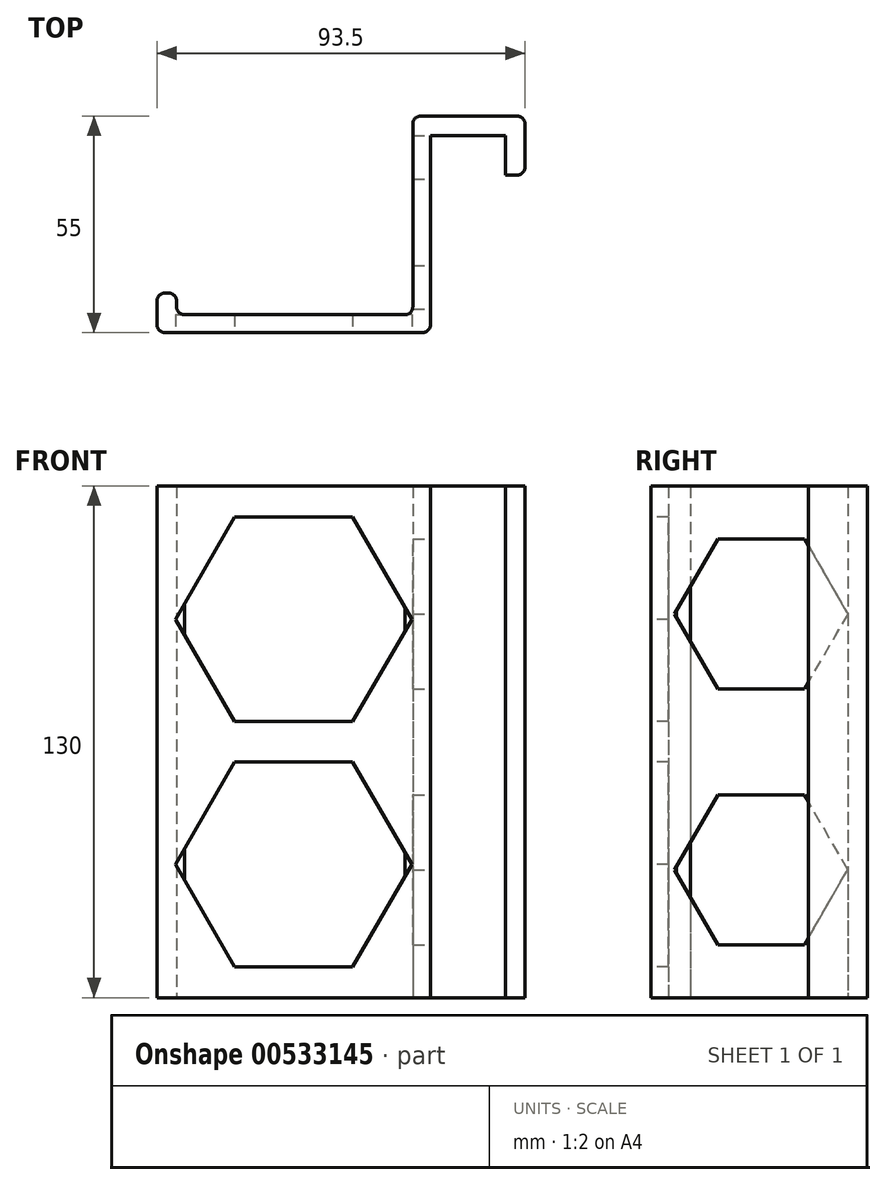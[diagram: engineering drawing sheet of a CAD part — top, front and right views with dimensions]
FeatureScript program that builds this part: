
annotation { "Feature Type Name" : "Feature", "Feature Type Description" : "" }
export const myFeature = defineFeature(function(context is Context, id is Id, definition is map)
    precondition{}
    {
        {
            var Q0;
            Q0=qCreatedBy(makeId("Top.planeOp"),FACE);
            var sketch = newSketch(context, id + "F0", { "sketchPlane" : qUnion([Q0])});
            skLineSegment(sketch, "E0.bottom", {"start": v(0, 0) * mm, "end": v(2, 0) * mm});
            skLineSegment(sketch, "E0.top", {"start": v(-2.5, 51.6) * mm, "end": v(0, 51.6) * mm});
            skLineSegment(sketch, "E0.left", {"start": v(-4.5, 3.12) * mm, "end": v(-4.5, 49.6) * mm});
            skLineSegment(sketch, "E1.bottom", {"start": v(0, 51.6) * mm, "end": v(19, 51.6) * mm});
            skLineSegment(sketch, "E1.top", {"start": v(0, 46.6) * mm, "end": v(19, 46.6) * mm});
            skLineSegment(sketch, "E1.left", {"start": v(0, 51.6) * mm, "end": v(0, 46.6) * mm});
            skLineSegment(sketch, "E1.right", {"start": v(19, 51.6) * mm, "end": v(19, 46.6) * mm});
            skLineSegment(sketch, "E2.bottom", {"start": v(19, 51.6) * mm, "end": v(22, 51.6) * mm});
            skLineSegment(sketch, "E2.top", {"start": v(19, 36.6) * mm, "end": v(22, 36.6) * mm});
            skLineSegment(sketch, "E2.left", {"start": v(19, 51.6) * mm, "end": v(19, 36.6) * mm});
            skLineSegment(sketch, "E2.right", {"start": v(24, 49.6) * mm, "end": v(24, 38.6) * mm});
            skLineSegment(sketch, "E3.bottom", {"start": v(-6.5, 1.12) * mm, "end": v(-62.5, 1.12) * mm});
            skLineSegment(sketch, "E4.bottom", {"start": v(-2, -3.4) * mm, "end": v(-67.5, -3.4) * mm});
            skLineSegment(sketch, "E4.top", {"start": v(-66.5, 6.6) * mm, "end": v(-67.5, 6.6) * mm});
            skLineSegment(sketch, "E4.left", {"start": v(-64.5, 3.12) * mm, "end": v(-64.5, 4.6) * mm});
            skLineSegment(sketch, "E4.right", {"start": v(-69.5, -1.4) * mm, "end": v(-69.5, 4.6) * mm});
            skPoint(sketch, "E5.visualSharp", {"position": v(-69.5, -3.4) * mm});
            skArc(sketch, "E5.filletArc", {"start": v(-69.5, -1.4) * mm, "mid": v(-68.91, -2.8) * mm, "end": v(-67.5, -3.4) * mm});
            skPoint(sketch, "E6.visualSharp", {"position": v(-69.5, 6.6) * mm});
            skArc(sketch, "E6.filletArc", {"start": v(-67.5, 6.6) * mm, "mid": v(-68.91, 6.02) * mm, "end": v(-69.5, 4.6) * mm});
            skPoint(sketch, "E7.visualSharp", {"position": v(-4.5, 51.6) * mm});
            skArc(sketch, "E7.filletArc", {"start": v(-2.5, 51.6) * mm, "mid": v(-3.91, 51.02) * mm, "end": v(-4.5, 49.6) * mm});
            skPoint(sketch, "E8.visualSharp", {"position": v(24, 51.6) * mm});
            skArc(sketch, "E8.filletArc", {"start": v(24, 49.6) * mm, "mid": v(23.41, 51.02) * mm, "end": v(22, 51.6) * mm});
            skPoint(sketch, "E9.visualSharp", {"position": v(24, 36.6) * mm});
            skArc(sketch, "E9.filletArc", {"start": v(22, 36.6) * mm, "mid": v(23.41, 37.2) * mm, "end": v(24, 38.6) * mm});
            skPoint(sketch, "E10.visualSharp", {"position": v(-64.5, 6.6) * mm});
            skArc(sketch, "E10.filletArc", {"start": v(-64.5, 4.6) * mm, "mid": v(-65.09, 6.02) * mm, "end": v(-66.5, 6.6) * mm});
            skLineSegment(sketch, "E11", {"start": v(0, 46.6) * mm, "end": v(0, -1.4) * mm});
            skPoint(sketch, "E12.visualSharp", {"position": v(-64.5, 1.12) * mm});
            skArc(sketch, "E12.filletArc", {"start": v(-64.5, 3.12) * mm, "mid": v(-63.91, 1.7) * mm, "end": v(-62.5, 1.12) * mm});
            skPoint(sketch, "E13.visualSharp", {"position": v(-4.5, 1.12) * mm});
            skArc(sketch, "E13.filletArc", {"start": v(-6.5, 1.12) * mm, "mid": v(-5.09, 1.7) * mm, "end": v(-4.5, 3.12) * mm});
            skPoint(sketch, "E14.visualSharp", {"position": v(0, -3.4) * mm});
            skArc(sketch, "E14.filletArc", {"start": v(-2, -3.4) * mm, "mid": v(-0.59, -2.8) * mm, "end": v(0, -1.4) * mm});
            skSolve(sketch);
        }
        {
            var Q0;
            Q0=makeQuery(id+"F0.imprint","IMPRINT",FACE,{"disambiguationData":[TD([[makeQuery(id+"F0.imprint","IMPRINT",EDGE,{"derivedFrom":sQuery(id+"F0.wireOp",EDGE,"E0.top")}),-1.0]])]});
            var Q1;
            {var subQ0=sQuery(id+"F0.wireOp",EDGE,"E1.bottom");Q1=makeQuery(id+"F0.imprint","IMPRINT",FACE,{"disambiguationData":[TD([[makeQuery(id+"F0.imprint","IMPRINT",EDGE,{"derivedFrom":subQ0}),-1.0]])]});}
            var Q2;
            {var subQ3=sQuery(id+"F0.wireOp",EDGE,"E2.bottom");Q2=makeQuery(id+"F0.imprint","IMPRINT",FACE,{"disambiguationData":[TD([[makeQuery(id+"F0.imprint","IMPRINT",EDGE,{"derivedFrom":subQ3}),-1.0]])]});}
            extrude(context, id + "F1", {"entities" : qUnion([Q0, Q1, Q2]), "depth" : 130 * mm, "offsetDistance" : 25 * mm});
        }
        {
            var Q0;
            Q0=makeQuery(id+"F1.opExtrude","SWEPT_FACE",FACE,{"disambiguationData":[OSD([sQuery(id+"F0.wireOp",EDGE,"E4.bottom")])]});
            var sketch = newSketch(context, id + "F2", { "sketchPlane" : qUnion([Q0])});
            skLineSegment(sketch, "E15", {"start": v(-64.75, 96.13) * mm, "end": v(-49.75, 122.11) * mm});
            skLineSegment(sketch, "E16", {"start": v(-49.75, 122.11) * mm, "end": v(-19.75, 122.11) * mm});
            skLineSegment(sketch, "E17", {"start": v(-19.75, 122.11) * mm, "end": v(-4.75, 96.13) * mm});
            skLineSegment(sketch, "E18", {"start": v(-4.75, 96.13) * mm, "end": v(-19.75, 70.15) * mm});
            skLineSegment(sketch, "E19", {"start": v(-19.75, 70.15) * mm, "end": v(-49.75, 70.15) * mm});
            skLineSegment(sketch, "E20", {"start": v(-49.75, 70.15) * mm, "end": v(-64.75, 96.13) * mm});
            skLineSegment(sketch, "E21", {"start": v(-67.5, 65) * mm, "end": v(-2, 65) * mm, "construction": true});
            skLineSegment(sketch, "E22", {"start": v(-34.75, 130) * mm, "end": v(-34.75, 0) * mm, "construction": true});
            skLineSegment(sketch, "E23.MirrorCS", {"start": v(-64.75, 33.87) * mm, "end": v(-49.75, 7.89) * mm});
            skLineSegment(sketch, "E24.MirrorCS", {"start": v(-19.75, 7.89) * mm, "end": v(-4.75, 33.87) * mm});
            skLineSegment(sketch, "E25.MirrorCS", {"start": v(-49.75, 7.89) * mm, "end": v(-19.75, 7.89) * mm});
            skLineSegment(sketch, "E26.MirrorCS", {"start": v(-4.75, 33.87) * mm, "end": v(-19.75, 59.85) * mm});
            skLineSegment(sketch, "E27.MirrorCS", {"start": v(-49.75, 59.85) * mm, "end": v(-64.75, 33.87) * mm});
            skLineSegment(sketch, "E28.MirrorCS", {"start": v(-19.75, 59.85) * mm, "end": v(-49.75, 59.85) * mm});
            skSolve(sketch);
        }
        {
            var Q0;
            Q0=makeQuery(id+"F2.imprint","IMPRINT",FACE,{"disambiguationData":[TD([[makeQuery(id+"F2.imprint","IMPRINT",EDGE,{"derivedFrom":sQuery(id+"F2.wireOp",EDGE,"E15")}),-1.0]])]});
            var Q1;
            Q1=makeQuery(id+"F2.imprint","IMPRINT",FACE,{"disambiguationData":[TD([[makeQuery(id+"F2.imprint","IMPRINT",EDGE,{"derivedFrom":sQuery(id+"F2.wireOp",EDGE,"E23.MirrorCS")}),1.0]])]});
            var Q2;
            Q2=makeQuery(id+"F1.opExtrude","SWEPT_FACE",FACE,{"disambiguationData":[OSD([sQuery(id+"F0.wireOp",EDGE,"E3.bottom")])]});
            extrude(context, id + "F3", {"entities" : qUnion([Q0, Q1]), "operationType" : NewBodyOperationType.REMOVE, "endBound" : BoundingType.UP_TO_SURFACE, "oppositeDirection" : true, "depth" : 25 * mm, "endBoundEntityFace" : qUnion([Q2]), "offsetDistance" : 25 * mm});
        }
        {
            var Q0;
            Q0=makeQuery(id+"F1.opExtrude","SWEPT_FACE",FACE,{"disambiguationData":[OSD([sQuery(id+"F0.wireOp",EDGE,"E11")])]});
            var sketch = newSketch(context, id + "F4", { "sketchPlane" : qUnion([Q0])});
            skLineSegment(sketch, "E29", {"start": v(-1.4, 65) * mm, "end": v(46.6, 65) * mm, "construction": true});
            skCircle(sketch, "E30.cCircle", {"center": v(24.6, 97.5) * mm, "radius": 22 * mm, "construction": true});
            skLineSegment(sketch, "E30.0", {"start": v(46.6, 97.5) * mm, "end": v(35.6, 78.45) * mm});
            skLineSegment(sketch, "E30.1", {"start": v(35.6, 78.45) * mm, "end": v(13.6, 78.45) * mm});
            skLineSegment(sketch, "E30.2", {"start": v(13.6, 78.45) * mm, "end": v(2.6, 97.5) * mm});
            skLineSegment(sketch, "E30.3", {"start": v(2.6, 97.5) * mm, "end": v(13.6, 116.55) * mm});
            skLineSegment(sketch, "E30.4", {"start": v(13.6, 116.55) * mm, "end": v(35.6, 116.55) * mm});
            skLineSegment(sketch, "E30.5", {"start": v(35.6, 116.55) * mm, "end": v(46.6, 97.5) * mm});
            skLineSegment(sketch, "E31", {"start": v(22.6, 65) * mm, "end": v(22.6, 130) * mm, "construction": true});
            skLineSegment(sketch, "E32", {"start": v(22.6, 97.5) * mm, "end": v(9.8, 97.5) * mm, "construction": true});
            skPoint(sketch, "E32.endSnap0", {"position": v(22.6, 97.5) * mm});
            skLineSegment(sketch, "E33.MirrorCS", {"start": v(13.6, 78.45) * mm, "end": v(35.6, 78.45) * mm});
            skLineSegment(sketch, "E34.MirrorCS", {"start": v(2.6, 97.5) * mm, "end": v(13.6, 78.45) * mm});
            skLineSegment(sketch, "E35.MirrorCS", {"start": v(13.6, 51.55) * mm, "end": v(35.6, 51.55) * mm});
            skLineSegment(sketch, "E36.MirrorCS", {"start": v(2.6, 32.5) * mm, "end": v(13.6, 51.55) * mm});
            skLineSegment(sketch, "E37.MirrorCS", {"start": v(2.6, 32.5) * mm, "end": v(13.6, 13.45) * mm});
            skLineSegment(sketch, "E38.MirrorCS", {"start": v(13.6, 13.45) * mm, "end": v(35.6, 13.45) * mm});
            skLineSegment(sketch, "E39.MirrorCS", {"start": v(46.6, 32.5) * mm, "end": v(35.6, 51.55) * mm});
            skLineSegment(sketch, "E40.MirrorCS", {"start": v(35.6, 13.45) * mm, "end": v(46.6, 32.5) * mm});
            skSolve(sketch);
        }
        {
            var Q0;
            Q0 = qSketchRegion(id + "F4", true);
            var Q1;
            Q1=makeQuery(id+"F1.opExtrude","SWEPT_FACE",FACE,{"disambiguationData":[OSD([sQuery(id+"F0.wireOp",EDGE,"E0.left")])]});
            extrude(context, id + "F5", {"entities" : qUnion([Q0]), "operationType" : NewBodyOperationType.REMOVE, "endBound" : BoundingType.UP_TO_SURFACE, "oppositeDirection" : true, "depth" : 25 * mm, "endBoundEntityFace" : qUnion([Q1]), "offsetDistance" : 25 * mm});
        }
    });
